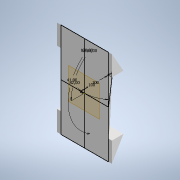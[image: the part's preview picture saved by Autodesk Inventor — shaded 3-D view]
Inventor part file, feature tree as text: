
AUTODESK INVENTOR PART (.ipt)
format: ipt  version: 2022 (Build 260153000, 153)  size: 119,296 bytes
history: native  units: mm
features: sketch x5, other x2, extrude x2, projected_geometry x1
ambient origin geometry x8: Origin, YZ Plane, XZ Plane, XY Plane, X Axis, Y Axis, Z Axis, Center Point
bodies: Body1 (feature_tree)
feature tree (10):
  other  "Твердое тело1"
  sketch  "Эскиз1"
  sketch  "Эскиз2"
  other  "РабПлоскость1"
  sketch  "Эскиз3"
  extrude  "Выдавливание1"  TaperAngle=120.0deg  [1 undecoded]
  extrude  "Выдавливание2"  TaperAngle=60.0deg  [1 undecoded]
  sketch  "Эскиз4"
  sketch  "Эскиз5"
  projected_geometry  "Спроецированная петля1"
note: 2 required parameter values undecoded (feature->parameter linkage not recoverable at this tier; creation-order binding heuristic only, values carry confidence <= 0.55)
